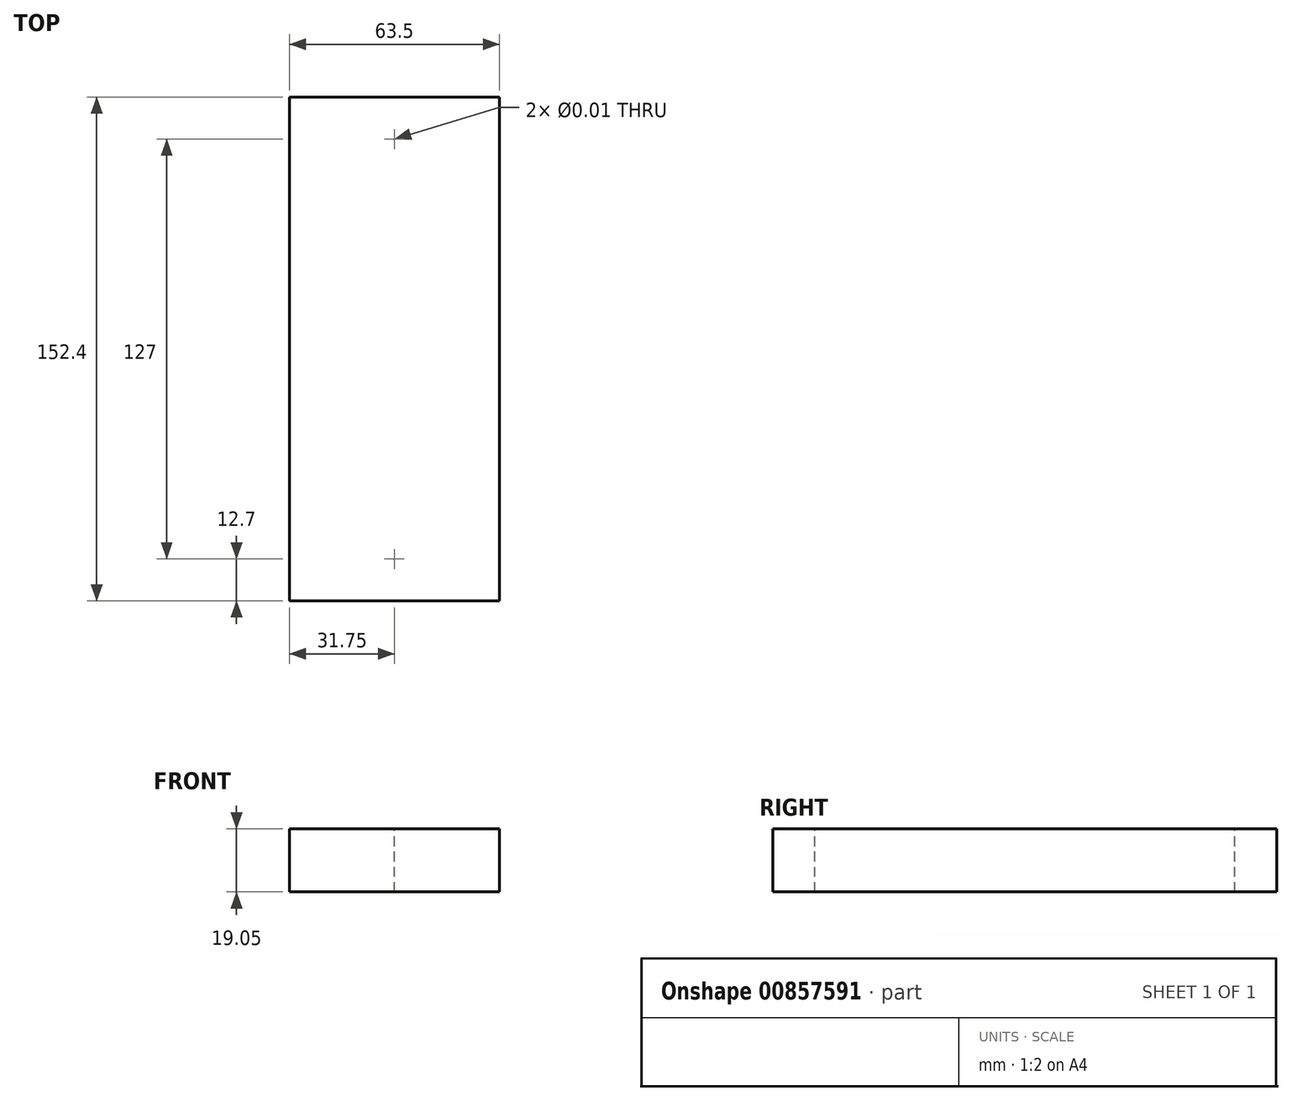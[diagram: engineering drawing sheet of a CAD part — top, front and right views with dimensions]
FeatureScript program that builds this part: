
annotation { "Feature Type Name" : "Feature", "Feature Type Description" : "" }
export const myFeature = defineFeature(function(context is Context, id is Id, definition is map)
    precondition{}
    {
        {
            var Q0;
            Q0=qCreatedBy(makeId("Top.planeOp"),FACE);
            var sketch = newSketch(context, id + "F0", { "sketchPlane" : qUnion([Q0])});
            skLineSegment(sketch, "E0.bottom", {"start": v(31.75, 76.2) * mm, "end": v(-31.75, 76.2) * mm});
            skLineSegment(sketch, "E0.top", {"start": v(31.75, -76.2) * mm, "end": v(-31.75, -76.2) * mm});
            skLineSegment(sketch, "E0.left", {"start": v(31.75, 76.2) * mm, "end": v(31.75, -76.2) * mm});
            skLineSegment(sketch, "E0.right", {"start": v(-31.75, 76.2) * mm, "end": v(-31.75, -76.2) * mm});
            skPoint(sketch, "E0.middle", {"position": v(0, 0) * mm});
            skSolve(sketch);
        }
        {
            var Q0;
            Q0=makeQuery(id+"F0.imprint","IMPRINT",FACE,{"disambiguationData":[TD([[makeQuery(id+"F0.imprint","IMPRINT",EDGE,{"derivedFrom":sQuery(id+"F0.wireOp",EDGE,"E0.bottom")}),1.0]])]});
            extrude(context, id + "F1", {"entities" : qUnion([Q0]), "depth" : 19.05 * mm, "offsetDistance" : 25.4 * mm});
        }
        {
            var Q0;
            Q0=makeQuery(id+"F1.opExtrude","CAP_FACE",FACE,{"disambiguationData":[OSD([sQuery(id+"F0.wireOp",EDGE,"E0.bottom"),sQuery(id+"F0.wireOp",EDGE,"E0.top"),sQuery(id+"F0.wireOp",EDGE,"E0.left"),sQuery(id+"F0.wireOp",EDGE,"E0.right")])],"isStart":false});
            var sketch = newSketch(context, id + "F2", { "sketchPlane" : qUnion([Q0])});
            skPoint(sketch, "E1", {"position": v(0, -63.5) * mm});
            skPoint(sketch, "E1.positionSnap0", {"position": v(0, -76.2) * mm});
            skPoint(sketch, "E2", {"position": v(0, 63.5) * mm});
            skSolve(sketch);
        }
        {
            var Q0;
            Q0=sQuery(id+"F2.wireOp",VERTEX,"E1");
            var Q1;
            Q1=sQuery(id+"F2.wireOp",VERTEX,"E2");
            var Q2;
            Q2=makeQuery(id+"F1.opExtrude","SWEPT_BODY",BODY,{"disambiguationData":[OSD([sQuery(id+"F0.wireOp",EDGE,"E0.bottom"),sQuery(id+"F0.wireOp",EDGE,"E0.top"),sQuery(id+"F0.wireOp",EDGE,"E0.left"),sQuery(id+"F0.wireOp",EDGE,"E0.right")])]});
            hole(context, id + "F3", {"style" : HoleStyle.SIMPLE, "endStyle" : HoleEndStyle.BLIND, "standardTappedOrClearance" : lookupTablePath({ "standard" : "ANSI", "size" : "3/8 (0.38)", "type" : "Drilled" }), "standardBlindInLast" : lookupTablePath({ "standard" : "ANSI", "size" : "3/8", "type" : "Drilled" }), "holeDiameter" : 3 / 203.2 * mm, "majorDiameter" : 6.35 * mm, "holeDepth" : 19.05 * mm, "isTappedThrough" : true, "tappedDepth" : 30.48 * mm, "tapClearance" : 3, "locations" : qUnion([Q0, Q1]), "scope" : qUnion([Q2])});
        }
    });
